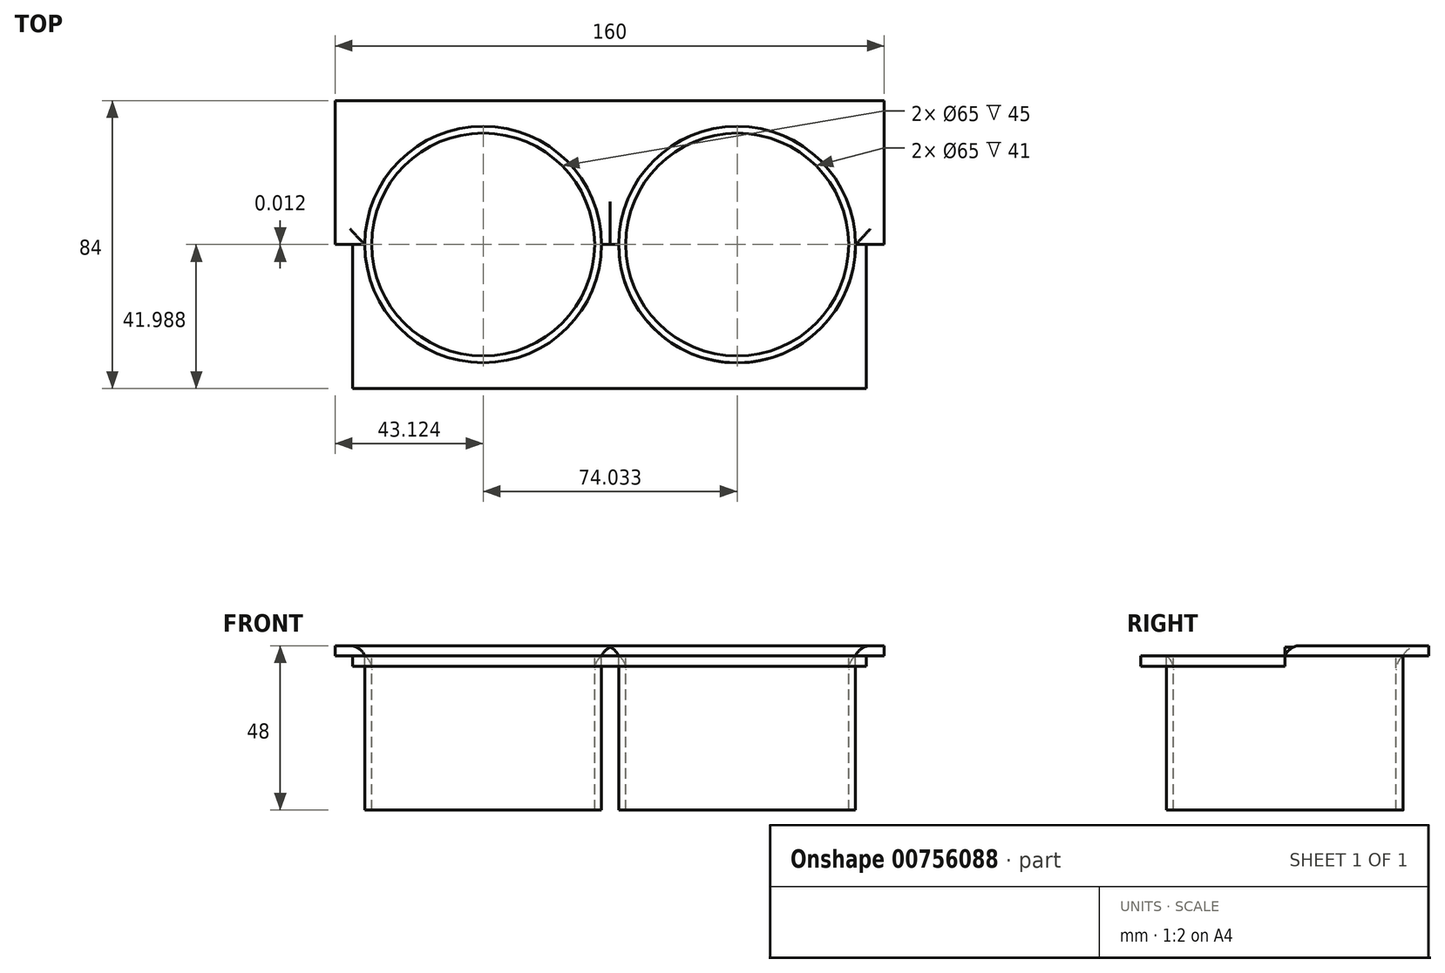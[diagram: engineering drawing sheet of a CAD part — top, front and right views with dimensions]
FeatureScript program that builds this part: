
annotation { "Feature Type Name" : "Feature", "Feature Type Description" : "" }
export const myFeature = defineFeature(function(context is Context, id is Id, definition is map)
    precondition{}
    {
        {
            var Q0;
            Q0=qCreatedBy(makeId("Top.planeOp"),FACE);
            var sketch = newSketch(context, id + "F0", { "sketchPlane" : qUnion([Q0])});
            skLineSegment(sketch, "E0.bottom", {"start": v(80, 42) * mm, "end": v(-80, 42) * mm});
            skLineSegment(sketch, "E0.top", {"start": v(80, -42) * mm, "end": v(-80, -42) * mm});
            skLineSegment(sketch, "E0.left", {"start": v(80, 42) * mm, "end": v(80, -42) * mm});
            skLineSegment(sketch, "E0.right", {"start": v(-80, 42) * mm, "end": v(-80, -42) * mm});
            skPoint(sketch, "E0.middle", {"position": v(0, 0) * mm});
            skCircle(sketch, "E1", {"center": v(-36.88, 0) * mm, "radius": 34.5 * mm});
            skCircle(sketch, "E2", {"center": v(37.16, -0.01) * mm, "radius": 34.5 * mm});
            skLineSegment(sketch, "E3", {"start": v(-80, 0) * mm, "end": v(-74.99, 0) * mm});
            skLineSegment(sketch, "E4", {"start": v(-74.99, 0) * mm, "end": v(-74.99, -42) * mm});
            skLineSegment(sketch, "E5", {"start": v(80, 0) * mm, "end": v(74.8, 0) * mm});
            skLineSegment(sketch, "E6", {"start": v(74.8, 0) * mm, "end": v(74.8, -42) * mm});
            skLineSegment(sketch, "E7", {"start": v(-74.99, 0) * mm, "end": v(-71.38, 0) * mm});
            skLineSegment(sketch, "E8", {"start": v(-2.38, 0) * mm, "end": v(2.66, 0) * mm});
            skLineSegment(sketch, "E9", {"start": v(74.8, 0) * mm, "end": v(71.66, 0) * mm});
            skCircle(sketch, "E10.0", {"center": v(-36.88, 0) * mm, "radius": 32.5 * mm});
            skCircle(sketch, "E11.0", {"center": v(37.16, -0.01) * mm, "radius": 32.5 * mm});
            skSolve(sketch);
        }
        {
            var Q0;
            {var subQ0=sQuery(id+"F0.wireOp",EDGE,"E1");var subQ1=makeQuery(id+"F0.imprint","INTERSECT",VERTEX,{"derivedFrom":[subQ0,sQuery(id+"F0.wireOp",EDGE,"E7")]});Q0=makeQuery(id+"F0.imprint","IMPRINT",FACE,{"disambiguationData":[TD([[makeQuery(id+"F0.imprint","IMPRINT",EDGE,{"disambiguationData":[TD([[subQ1,1.0]])],"derivedFrom":subQ0}),1.0]])]});}
            var Q1;
            {var subQ0=sQuery(id+"F0.wireOp",EDGE,"E2");var subQ1=makeQuery(id+"F0.imprint","INTERSECT",VERTEX,{"derivedFrom":[subQ0,sQuery(id+"F0.wireOp",EDGE,"E8")]});Q1=makeQuery(id+"F0.imprint","IMPRINT",FACE,{"disambiguationData":[TD([[makeQuery(id+"F0.imprint","IMPRINT",EDGE,{"disambiguationData":[TD([[subQ1,1.0]])],"derivedFrom":subQ0}),1.0]])]});}
            extrude(context, id + "F1", {"entities" : qUnion([Q0, Q1]), "oppositeDirection" : true, "depth" : 45 * mm, "offsetDistance" : 25 * mm});
        }
        {
            var Q0;
            {var subQ0=sQuery(id+"F0.wireOp",EDGE,"E4");Q0=makeQuery(id+"F0.imprint","IMPRINT",FACE,{"disambiguationData":[TD([[makeQuery(id+"F0.imprint","IMPRINT",EDGE,{"derivedFrom":subQ0}),1.0]])]});}
            extrude(context, id + "F2", {"entities" : qUnion([Q0]), "oppositeDirection" : true, "depth" : 3 * mm, "offsetDistance" : 25 * mm});
        }
        {
            var Q0;
            {var subQ4=sQuery(id+"F0.wireOp",EDGE,"E0.bottom");Q0=makeQuery(id+"F0.imprint","IMPRINT",FACE,{"disambiguationData":[TD([[makeQuery(id+"F0.imprint","IMPRINT",EDGE,{"derivedFrom":subQ4}),1.0]])]});}
            extrude(context, id + "F3", {"entities" : qUnion([Q0]), "depth" : 3 * mm, "offsetDistance" : 25 * mm});
        }
        {
            var Q0;
            Q0=makeQuery(id+"F0.imprint","IMPRINT",FACE,{"disambiguationData":[TD([[makeQuery(id+"F0.imprint","IMPRINT",EDGE,{"derivedFrom":sQuery(id+"F0.wireOp",EDGE,"E10.0")}),-1.0]])]});
            var Q1;
            Q1=makeQuery(id+"F0.imprint","IMPRINT",FACE,{"disambiguationData":[TD([[makeQuery(id+"F0.imprint","IMPRINT",EDGE,{"derivedFrom":sQuery(id+"F0.wireOp",EDGE,"E11.0")}),-1.0]])]});
            extrude(context, id + "F4", {"entities" : qUnion([Q0, Q1]), "oppositeDirection" : true, "depth" : 45 * mm, "offsetDistance" : 25 * mm});
        }
        {
            var Q0;
            Q0=makeQuery(id+"F1.opExtrude","CAP_EDGE",EDGE,{"disambiguationData":[OSD([sQuery(id+"F0.wireOp",EDGE,"E10.0")])],"isStart":true});
            var Q1;
            Q1=makeQuery(id+"F3.opExtrude","CAP_EDGE",EDGE,{"disambiguationData":[OSD([sQuery(id+"F0.wireOp",EDGE,"E1")])],"isStart":false});
            var Q2;
            Q2=makeQuery(id+"F1.opExtrude","CAP_EDGE",EDGE,{"disambiguationData":[OSD([sQuery(id+"F0.wireOp",EDGE,"E11.0")])],"isStart":true});
            var Q3;
            Q3=makeQuery(id+"F3.opExtrude","CAP_EDGE",EDGE,{"disambiguationData":[OSD([sQuery(id+"F0.wireOp",EDGE,"E2")])],"isStart":false});
            var Q4;
            Q4=makeQuery(id+"F3.opExtrude","CAP_EDGE",EDGE,{"disambiguationData":[OSD([sQuery(id+"F0.wireOp",EDGE,"E5"),sQuery(id+"F0.wireOp",EDGE,"E9")])],"isStart":false});
            var Q5;
            Q5=makeQuery(id+"F3.opExtrude","CAP_EDGE",EDGE,{"disambiguationData":[OSD([sQuery(id+"F0.wireOp",EDGE,"E3"),sQuery(id+"F0.wireOp",EDGE,"E7")])],"isStart":false});
            fillet(context, id + "F5", {"entities" : qUnion([Q0, Q1, Q2, Q3, Q4, Q5]), "radius" : 5 * mm, "tangentPropagation" : true, "allowEdgeOverflow" : false});
        }
    });
